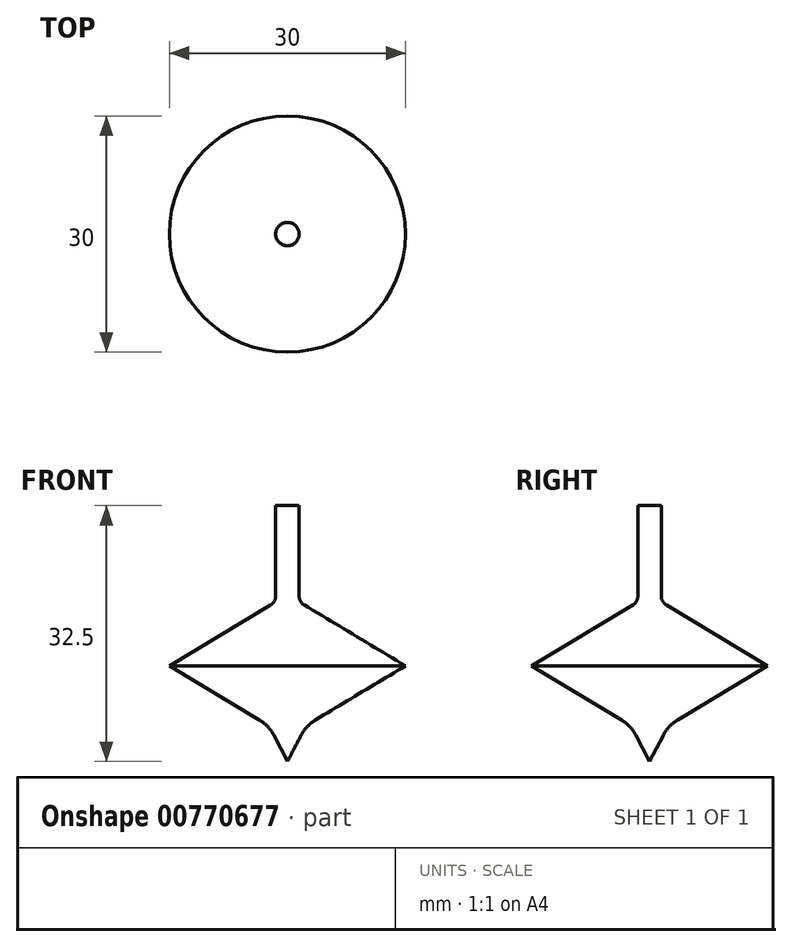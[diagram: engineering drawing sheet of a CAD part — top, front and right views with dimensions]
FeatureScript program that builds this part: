
annotation { "Feature Type Name" : "Feature", "Feature Type Description" : "" }
export const myFeature = defineFeature(function(context is Context, id is Id, definition is map)
    precondition{}
    {
        {
            var Q0;
            Q0=qCreatedBy(makeId("Front.planeOp"),FACE);
            var sketch = newSketch(context, id + "F0", { "sketchPlane" : qUnion([Q0])});
            skLineSegment(sketch, "E0", {"start": v(-15, 0) * mm, "end": v(0, 0) * mm});
            skLineSegment(sketch, "E1", {"start": v(-15, 0) * mm, "end": v(0, 9.01) * mm});
            skLineSegment(sketch, "E2", {"start": v(0, 9.01) * mm, "end": v(0, 0) * mm});
            skLineSegment(sketch, "E3", {"start": v(0, 0) * mm, "end": v(0, -9) * mm});
            skLineSegment(sketch, "E4", {"start": v(-15, 0) * mm, "end": v(0, -9) * mm});
            skLineSegment(sketch, "E5", {"start": v(-2.38, -7.58) * mm, "end": v(0, -12.15) * mm});
            skLineSegment(sketch, "E6", {"start": v(0, -12.15) * mm, "end": v(0, -9) * mm});
            skLineSegment(sketch, "E7", {"start": v(0, 20.35) * mm, "end": v(0, 9.01) * mm});
            skLineSegment(sketch, "E8", {"start": v(0, 20.35) * mm, "end": v(-1.49, 20.35) * mm});
            skLineSegment(sketch, "E9", {"start": v(-1.49, 20.35) * mm, "end": v(-1.49, 8.12) * mm});
            skSolve(sketch);
        }
        {
            var Q0;
            {var subQ0=sQuery(id+"F0.wireOp",EDGE,"E7");Q0=makeQuery(id+"F0.imprint","IMPRINT",FACE,{"disambiguationData":[TD([[makeQuery(id+"F0.imprint","IMPRINT",EDGE,{"derivedFrom":subQ0}),-1.0]])]});}
            var Q1;
            {var subQ0=sQuery(id+"F0.wireOp",EDGE,"E0");Q1=makeQuery(id+"F0.imprint","IMPRINT",FACE,{"disambiguationData":[TD([[makeQuery(id+"F0.imprint","IMPRINT",EDGE,{"derivedFrom":subQ0}),1.0]])]});}
            var Q2;
            {var subQ0=sQuery(id+"F0.wireOp",EDGE,"E0");Q2=makeQuery(id+"F0.imprint","IMPRINT",FACE,{"disambiguationData":[TD([[makeQuery(id+"F0.imprint","IMPRINT",EDGE,{"derivedFrom":subQ0}),-1.0]])]});}
            var Q3;
            {var subQ2=sQuery(id+"F0.wireOp",EDGE,"E5");Q3=makeQuery(id+"F0.imprint","IMPRINT",FACE,{"disambiguationData":[TD([[makeQuery(id+"F0.imprint","IMPRINT",EDGE,{"derivedFrom":subQ2}),1.0]])]});}
            var Q4;
            Q4=sQuery(id+"F0.wireOp",EDGE,"E3");
            revolve(context, id + "F1", {"surfaceOperationType" : NewSurfaceOperationType.NEW, "entities" : qUnion([Q0, Q1, Q2, Q3]), "axis" : qUnion([Q4]), "revolveType" : RevolveType.FULL});
        }
        {
            var Q0;
            Q0=makeQuery(id+"F1.opRevolve","SWEPT_EDGE",EDGE,{"disambiguationData":[OSD([sQuery(id+"F0.wireOp",EDGE,"E4"),sQuery(id+"F0.wireOp",EDGE,"E5")])]});
            fillet(context, id + "F2", {"entities" : qUnion([Q0]), "radius" : 5 * mm, "tangentPropagation" : true, "allowEdgeOverflow" : false});
        }
        {
            var Q0;
            Q0=makeQuery(id+"F1.opRevolve","SWEPT_EDGE",EDGE,{"disambiguationData":[OSD([sQuery(id+"F0.wireOp",EDGE,"E1"),sQuery(id+"F0.wireOp",EDGE,"E9")])]});
            fillet(context, id + "F3", {"entities" : qUnion([Q0]), "radius" : 1.34 * mm, "tangentPropagation" : true, "allowEdgeOverflow" : false});
        }
    });
